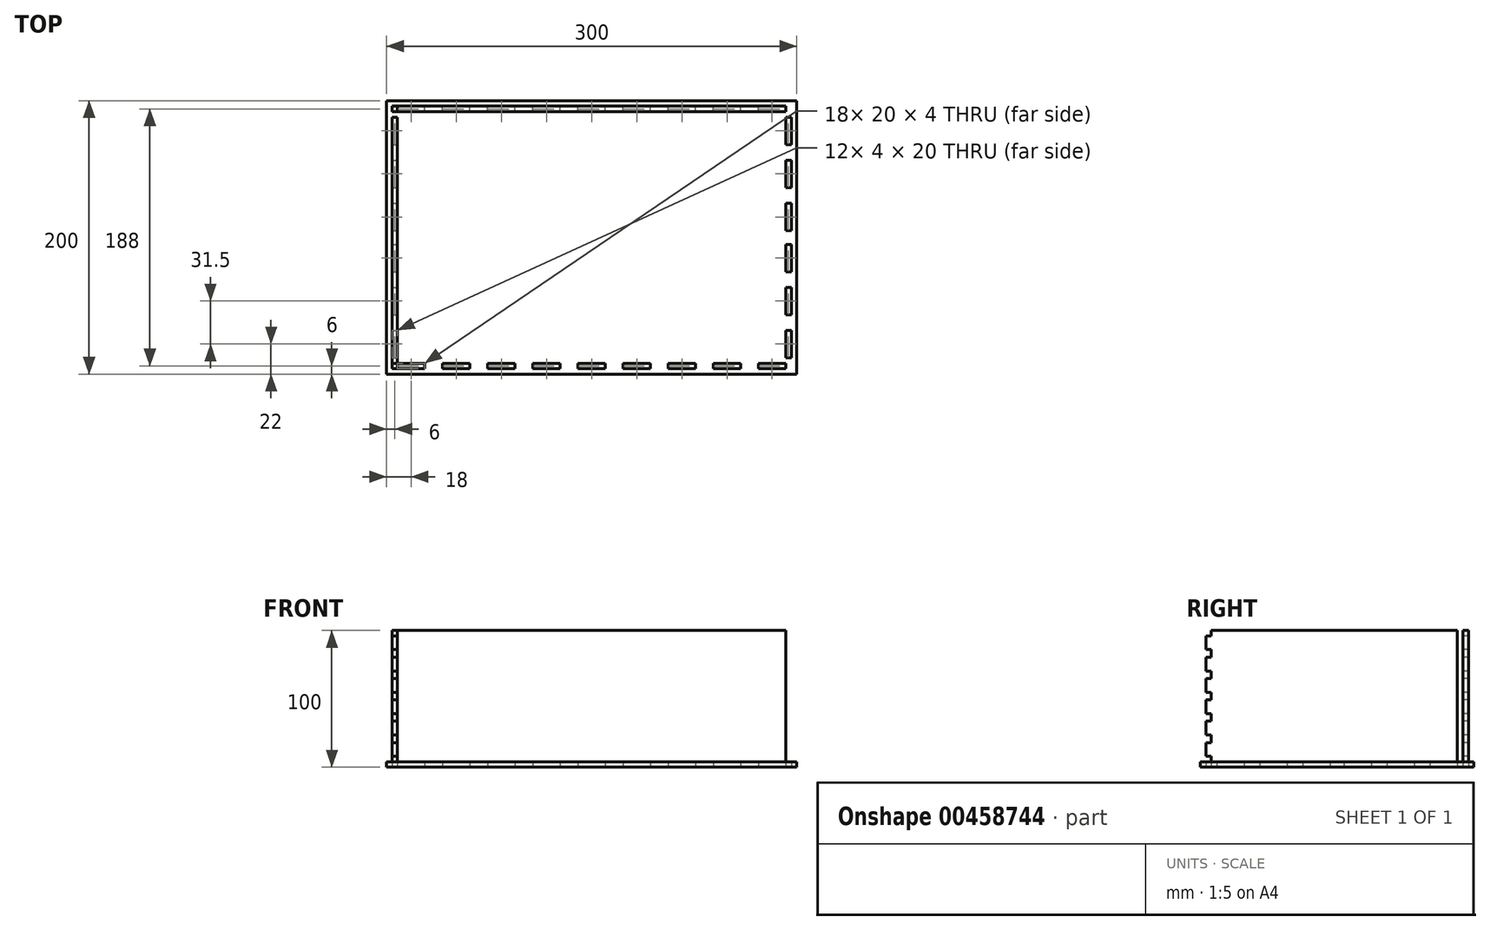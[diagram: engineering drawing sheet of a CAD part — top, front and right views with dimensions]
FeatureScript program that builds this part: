
annotation { "Feature Type Name" : "Feature", "Feature Type Description" : "" }
export const myFeature = defineFeature(function(context is Context, id is Id, definition is map)
    precondition{}
    {
        {
            assignVariable(context, id + "F0", {"name" : "w", "anyValue" : 4});
        }
        {
            var Q0;
            Q0=qCreatedBy(makeId("Top.planeOp"),FACE);
            var sketch = newSketch(context, id + "F1", { "sketchPlane" : qUnion([Q0])});
            skLineSegment(sketch, "E0.bottom", {"start": v(150, -100) * mm, "end": v(-150, -100) * mm});
            skLineSegment(sketch, "E0.top", {"start": v(150, 100) * mm, "end": v(-150, 100) * mm});
            skLineSegment(sketch, "E0.left", {"start": v(150, -100) * mm, "end": v(150, 100) * mm});
            skLineSegment(sketch, "E0.right", {"start": v(-150, -100) * mm, "end": v(-150, 100) * mm});
            skPoint(sketch, "E0.middle", {"position": v(0, 0) * mm});
            skLineSegment(sketch, "E1.0", {"start": v(142, 92) * mm, "end": v(-142, 92) * mm, "construction": true});
            skLineSegment(sketch, "E1.1", {"start": v(142, -92) * mm, "end": v(142, 92) * mm, "construction": true});
            skLineSegment(sketch, "E1.2", {"start": v(142, -92) * mm, "end": v(-142, -92) * mm, "construction": true});
            skLineSegment(sketch, "E1.3", {"start": v(-142, -92) * mm, "end": v(-142, 92) * mm, "construction": true});
            skLineSegment(sketch, "E2", {"start": v(-142, 0) * mm, "end": v(142, 0) * mm, "construction": true});
            skLineSegment(sketch, "E3", {"start": v(0, 92) * mm, "end": v(0, -92) * mm, "construction": true});
            skLineSegment(sketch, "E4.bottom", {"start": v(-142, 92) * mm, "end": v(-122, 92) * mm});
            skLineSegment(sketch, "E4.top", {"start": v(-142, 96) * mm, "end": v(-122, 96) * mm});
            skLineSegment(sketch, "E4.left", {"start": v(-142, 92) * mm, "end": v(-142, 96) * mm});
            skLineSegment(sketch, "E4.right", {"start": v(-122, 92) * mm, "end": v(-122, 96) * mm});
            skLineSegment(sketch, "E5.1.0.0", {"start": v(-109, 96) * mm, "end": v(-89, 96) * mm});
            skLineSegment(sketch, "E5.1.0.1", {"start": v(-109, 92) * mm, "end": v(-109, 96) * mm});
            skLineSegment(sketch, "E5.1.0.2", {"start": v(-89, 92) * mm, "end": v(-89, 96) * mm});
            skLineSegment(sketch, "E5.1.0.3", {"start": v(-109, 92) * mm, "end": v(-89, 92) * mm});
            skLineSegment(sketch, "E5.2.0.0", {"start": v(-76, 96) * mm, "end": v(-56, 96) * mm});
            skLineSegment(sketch, "E5.2.0.1", {"start": v(-76, 92) * mm, "end": v(-76, 96) * mm});
            skLineSegment(sketch, "E5.2.0.2", {"start": v(-56, 92) * mm, "end": v(-56, 96) * mm});
            skLineSegment(sketch, "E5.2.0.3", {"start": v(-76, 92) * mm, "end": v(-56, 92) * mm});
            skLineSegment(sketch, "E5.3.0.0", {"start": v(-43, 96) * mm, "end": v(-23, 96) * mm});
            skLineSegment(sketch, "E5.3.0.1", {"start": v(-43, 92) * mm, "end": v(-43, 96) * mm});
            skLineSegment(sketch, "E5.3.0.2", {"start": v(-23, 92) * mm, "end": v(-23, 96) * mm});
            skLineSegment(sketch, "E5.3.0.3", {"start": v(-43, 92) * mm, "end": v(-23, 92) * mm});
            skLineSegment(sketch, "E5.4.0.0", {"start": v(-10, 96) * mm, "end": v(10, 96) * mm});
            skLineSegment(sketch, "E5.4.0.1", {"start": v(-10, 92) * mm, "end": v(-10, 96) * mm});
            skLineSegment(sketch, "E5.4.0.2", {"start": v(10, 92) * mm, "end": v(10, 96) * mm});
            skLineSegment(sketch, "E5.4.0.3", {"start": v(-10, 92) * mm, "end": v(10, 92) * mm});
            skLineSegment(sketch, "E5.5.0.0", {"start": v(23, 96) * mm, "end": v(43, 96) * mm});
            skLineSegment(sketch, "E5.5.0.1", {"start": v(23, 92) * mm, "end": v(23, 96) * mm});
            skLineSegment(sketch, "E5.5.0.2", {"start": v(43, 92) * mm, "end": v(43, 96) * mm});
            skLineSegment(sketch, "E5.5.0.3", {"start": v(23, 92) * mm, "end": v(43, 92) * mm});
            skLineSegment(sketch, "E5.6.0.0", {"start": v(56, 96) * mm, "end": v(76, 96) * mm});
            skLineSegment(sketch, "E5.6.0.1", {"start": v(56, 92) * mm, "end": v(56, 96) * mm});
            skLineSegment(sketch, "E5.6.0.2", {"start": v(76, 92) * mm, "end": v(76, 96) * mm});
            skLineSegment(sketch, "E5.6.0.3", {"start": v(56, 92) * mm, "end": v(76, 92) * mm});
            skLineSegment(sketch, "E5.7.0.0", {"start": v(89, 96) * mm, "end": v(109, 96) * mm});
            skLineSegment(sketch, "E5.7.0.1", {"start": v(89, 92) * mm, "end": v(89, 96) * mm});
            skLineSegment(sketch, "E5.7.0.2", {"start": v(109, 92) * mm, "end": v(109, 96) * mm});
            skLineSegment(sketch, "E5.7.0.3", {"start": v(89, 92) * mm, "end": v(109, 92) * mm});
            skLineSegment(sketch, "E5.8.0.0", {"start": v(122, 96) * mm, "end": v(142, 96) * mm});
            skLineSegment(sketch, "E5.8.0.1", {"start": v(122, 92) * mm, "end": v(122, 96) * mm});
            skLineSegment(sketch, "E5.8.0.2", {"start": v(142, 92) * mm, "end": v(142, 96) * mm});
            skLineSegment(sketch, "E5.8.0.3", {"start": v(122, 92) * mm, "end": v(142, 92) * mm});
            skLineSegment(sketch, "E5.direction1", {"start": v(-142, 96) * mm, "end": v(-109, 96) * mm, "construction": true});
            skLineSegment(sketch, "E6.MirrorCS", {"start": v(-142, -92) * mm, "end": v(-142, -96) * mm});
            skLineSegment(sketch, "E7.MirrorCS", {"start": v(23, -92) * mm, "end": v(23, -96) * mm});
            skLineSegment(sketch, "E8.MirrorCS", {"start": v(-23, -92) * mm, "end": v(-23, -96) * mm});
            skLineSegment(sketch, "E9.MirrorCS", {"start": v(109, -92) * mm, "end": v(109, -96) * mm});
            skLineSegment(sketch, "E10.MirrorCS", {"start": v(10, -92) * mm, "end": v(10, -96) * mm});
            skLineSegment(sketch, "E11.MirrorCS", {"start": v(142, -92) * mm, "end": v(142, -96) * mm});
            skLineSegment(sketch, "E12.MirrorCS", {"start": v(43, -92) * mm, "end": v(43, -96) * mm});
            skLineSegment(sketch, "E13.MirrorCS", {"start": v(-89, -92) * mm, "end": v(-89, -96) * mm});
            skLineSegment(sketch, "E14.MirrorCS", {"start": v(76, -92) * mm, "end": v(76, -96) * mm});
            skLineSegment(sketch, "E15.MirrorCS", {"start": v(-56, -92) * mm, "end": v(-56, -96) * mm});
            skLineSegment(sketch, "E16.MirrorCS", {"start": v(-43, -92) * mm, "end": v(-43, -96) * mm});
            skLineSegment(sketch, "E17.MirrorCS", {"start": v(89, -92) * mm, "end": v(89, -96) * mm});
            skLineSegment(sketch, "E18.MirrorCS", {"start": v(-10, -92) * mm, "end": v(-10, -96) * mm});
            skLineSegment(sketch, "E19.MirrorCS", {"start": v(122, -92) * mm, "end": v(122, -96) * mm});
            skLineSegment(sketch, "E20.MirrorCS", {"start": v(-76, -92) * mm, "end": v(-76, -96) * mm});
            skLineSegment(sketch, "E21.MirrorCS", {"start": v(-109, -92) * mm, "end": v(-109, -96) * mm});
            skLineSegment(sketch, "E22.MirrorCS", {"start": v(-122, -92) * mm, "end": v(-122, -96) * mm});
            skLineSegment(sketch, "E23.MirrorCS", {"start": v(56, -92) * mm, "end": v(56, -96) * mm});
            skLineSegment(sketch, "E24.MirrorCS", {"start": v(-43, -92) * mm, "end": v(-23, -92) * mm});
            skLineSegment(sketch, "E25.MirrorCS", {"start": v(89, -92) * mm, "end": v(109, -92) * mm});
            skLineSegment(sketch, "E26.MirrorCS", {"start": v(23, -92) * mm, "end": v(43, -92) * mm});
            skLineSegment(sketch, "E27.MirrorCS", {"start": v(-109, -92) * mm, "end": v(-89, -92) * mm});
            skLineSegment(sketch, "E28.MirrorCS", {"start": v(56, -92) * mm, "end": v(76, -92) * mm});
            skLineSegment(sketch, "E29.MirrorCS", {"start": v(-76, -92) * mm, "end": v(-56, -92) * mm});
            skLineSegment(sketch, "E30.MirrorCS", {"start": v(-10, -92) * mm, "end": v(10, -92) * mm});
            skLineSegment(sketch, "E31.MirrorCS", {"start": v(122, -92) * mm, "end": v(142, -92) * mm});
            skLineSegment(sketch, "E32.MirrorCS", {"start": v(-142, -96) * mm, "end": v(-122, -96) * mm});
            skLineSegment(sketch, "E33.MirrorCS", {"start": v(-142, -92) * mm, "end": v(-122, -92) * mm});
            skLineSegment(sketch, "E34.MirrorCS", {"start": v(56, -96) * mm, "end": v(76, -96) * mm});
            skLineSegment(sketch, "E35.MirrorCS", {"start": v(-76, -96) * mm, "end": v(-56, -96) * mm});
            skLineSegment(sketch, "E36.MirrorCS", {"start": v(89, -96) * mm, "end": v(109, -96) * mm});
            skLineSegment(sketch, "E37.MirrorCS", {"start": v(-43, -96) * mm, "end": v(-23, -96) * mm});
            skLineSegment(sketch, "E38.MirrorCS", {"start": v(23, -96) * mm, "end": v(43, -96) * mm});
            skLineSegment(sketch, "E39.MirrorCS", {"start": v(-142, -96) * mm, "end": v(-109, -96) * mm, "construction": true});
            skLineSegment(sketch, "E40.MirrorCS", {"start": v(-10, -96) * mm, "end": v(10, -96) * mm});
            skLineSegment(sketch, "E41.MirrorCS", {"start": v(122, -96) * mm, "end": v(142, -96) * mm});
            skLineSegment(sketch, "E42.MirrorCS", {"start": v(-109, -96) * mm, "end": v(-89, -96) * mm});
            skLineSegment(sketch, "E43.bottom", {"start": v(-146, 88) * mm, "end": v(-142, 88) * mm});
            skLineSegment(sketch, "E43.top", {"start": v(-146, 68) * mm, "end": v(-142, 68) * mm});
            skLineSegment(sketch, "E43.left", {"start": v(-142, 88) * mm, "end": v(-142, 68) * mm});
            skLineSegment(sketch, "E43.right", {"start": v(-146, 88) * mm, "end": v(-146, 68) * mm});
            skLineSegment(sketch, "E44.0.1.0", {"start": v(-146, -5) * mm, "end": v(-146, -25) * mm});
            skLineSegment(sketch, "E44.0.1.1", {"start": v(-146, -5) * mm, "end": v(-142, -5) * mm});
            skLineSegment(sketch, "E44.0.1.2", {"start": v(-146, -25) * mm, "end": v(-142, -25) * mm});
            skLineSegment(sketch, "E44.0.1.3", {"start": v(-142, -5) * mm, "end": v(-142, -25) * mm});
            skLineSegment(sketch, "E44.1.0.0", {"start": v(-146, 56.5) * mm, "end": v(-146, 36.5) * mm});
            skLineSegment(sketch, "E44.1.0.1", {"start": v(-146, 56.5) * mm, "end": v(-142, 56.5) * mm});
            skLineSegment(sketch, "E44.1.0.2", {"start": v(-146, 36.5) * mm, "end": v(-142, 36.5) * mm});
            skLineSegment(sketch, "E44.1.0.3", {"start": v(-142, 56.5) * mm, "end": v(-142, 36.5) * mm});
            skLineSegment(sketch, "E44.1.1.0", {"start": v(-146, -36.5) * mm, "end": v(-146, -56.5) * mm});
            skLineSegment(sketch, "E44.1.1.1", {"start": v(-146, -36.5) * mm, "end": v(-142, -36.5) * mm});
            skLineSegment(sketch, "E44.1.1.2", {"start": v(-146, -56.5) * mm, "end": v(-142, -56.5) * mm});
            skLineSegment(sketch, "E44.1.1.3", {"start": v(-142, -36.5) * mm, "end": v(-142, -56.5) * mm});
            skLineSegment(sketch, "E44.2.0.0", {"start": v(-146, 25) * mm, "end": v(-146, 5) * mm});
            skLineSegment(sketch, "E44.2.0.1", {"start": v(-146, 25) * mm, "end": v(-142, 25) * mm});
            skLineSegment(sketch, "E44.2.0.2", {"start": v(-146, 5) * mm, "end": v(-142, 5) * mm});
            skLineSegment(sketch, "E44.2.0.3", {"start": v(-142, 25) * mm, "end": v(-142, 5) * mm});
            skLineSegment(sketch, "E44.2.1.0", {"start": v(-146, -68) * mm, "end": v(-146, -88) * mm});
            skLineSegment(sketch, "E44.2.1.1", {"start": v(-146, -68) * mm, "end": v(-142, -68) * mm});
            skLineSegment(sketch, "E44.2.1.2", {"start": v(-146, -88) * mm, "end": v(-142, -88) * mm});
            skLineSegment(sketch, "E44.2.1.3", {"start": v(-142, -68) * mm, "end": v(-142, -88) * mm});
            skLineSegment(sketch, "E44.direction1", {"start": v(-146, 68) * mm, "end": v(-146, 36.5) * mm, "construction": true});
            skLineSegment(sketch, "E44.direction2", {"start": v(-146, 68) * mm, "end": v(-146, -25) * mm, "construction": true});
            skLineSegment(sketch, "E45.MirrorCS", {"start": v(142, 92) * mm, "end": v(122, 92) * mm});
            skLineSegment(sketch, "E46.MirrorCS", {"start": v(146, -36.5) * mm, "end": v(142, -36.5) * mm});
            skLineSegment(sketch, "E47.MirrorCS", {"start": v(146, 56.5) * mm, "end": v(146, 36.5) * mm});
            skLineSegment(sketch, "E48.MirrorCS", {"start": v(146, -68) * mm, "end": v(142, -68) * mm});
            skLineSegment(sketch, "E49.MirrorCS", {"start": v(146, -5) * mm, "end": v(142, -5) * mm});
            skLineSegment(sketch, "E50.MirrorCS", {"start": v(146, 88) * mm, "end": v(142, 88) * mm});
            skLineSegment(sketch, "E51.MirrorCS", {"start": v(146, 56.5) * mm, "end": v(142, 56.5) * mm});
            skLineSegment(sketch, "E52.MirrorCS", {"start": v(146, -25) * mm, "end": v(142, -25) * mm});
            skLineSegment(sketch, "E53.MirrorCS", {"start": v(146, -88) * mm, "end": v(142, -88) * mm});
            skLineSegment(sketch, "E54.MirrorCS", {"start": v(146, -56.5) * mm, "end": v(142, -56.5) * mm});
            skLineSegment(sketch, "E55.MirrorCS", {"start": v(146, 68) * mm, "end": v(142, 68) * mm});
            skLineSegment(sketch, "E56.MirrorCS", {"start": v(146, 25) * mm, "end": v(142, 25) * mm});
            skLineSegment(sketch, "E57.MirrorCS", {"start": v(146, 36.5) * mm, "end": v(142, 36.5) * mm});
            skLineSegment(sketch, "E58.MirrorCS", {"start": v(146, 5) * mm, "end": v(142, 5) * mm});
            skLineSegment(sketch, "E59.MirrorCS", {"start": v(-142, 92) * mm, "end": v(142, 92) * mm, "construction": true});
            skLineSegment(sketch, "E60.MirrorCS", {"start": v(146, 68) * mm, "end": v(146, 36.5) * mm, "construction": true});
            skLineSegment(sketch, "E61.MirrorCS", {"start": v(146, 25) * mm, "end": v(146, 5) * mm});
            skLineSegment(sketch, "E62.MirrorCS", {"start": v(146, -5) * mm, "end": v(146, -25) * mm});
            skLineSegment(sketch, "E63.MirrorCS", {"start": v(142, -36.5) * mm, "end": v(142, -56.5) * mm});
            skLineSegment(sketch, "E64.MirrorCS", {"start": v(142, -5) * mm, "end": v(142, -25) * mm});
            skLineSegment(sketch, "E65.MirrorCS", {"start": v(142, -68) * mm, "end": v(142, -88) * mm});
            skLineSegment(sketch, "E66.MirrorCS", {"start": v(146, 68) * mm, "end": v(146, -25) * mm, "construction": true});
            skLineSegment(sketch, "E67.MirrorCS", {"start": v(146, -68) * mm, "end": v(146, -88) * mm});
            skLineSegment(sketch, "E68.MirrorCS", {"start": v(146, -36.5) * mm, "end": v(146, -56.5) * mm});
            skLineSegment(sketch, "E69.MirrorCS", {"start": v(146, 88) * mm, "end": v(146, 68) * mm});
            skLineSegment(sketch, "E70.MirrorCS", {"start": v(142, 25) * mm, "end": v(142, 5) * mm});
            skLineSegment(sketch, "E71.MirrorCS", {"start": v(142, 56.5) * mm, "end": v(142, 36.5) * mm});
            skLineSegment(sketch, "E72.MirrorCS", {"start": v(142, 88) * mm, "end": v(142, 68) * mm});
            skSolve(sketch);
        }
        {
            var Q0;
            Q0=makeQuery(id+"F1.imprint","IMPRINT",FACE,{"disambiguationData":[TD([[makeQuery(id+"F1.imprint","IMPRINT",EDGE,{"derivedFrom":sQuery(id+"F1.wireOp",EDGE,"E0.bottom")}),-1.0]])]});
            extrude(context, id + "F2", {"entities" : qUnion([Q0]), "depth" : (getVariable(context, 'w')) * mm});
        }
        {
            var Q0;
            Q0=makeQuery(id+"F1.imprint","IMPRINT",FACE,{"disambiguationData":[TD([[makeQuery(id+"F1.imprint","IMPRINT",EDGE,{"derivedFrom":sQuery(id+"F1.wireOp",EDGE,"E4.bottom")}),1.0]])]});
            var Q1;
            Q1=makeQuery(id+"F1.imprint","IMPRINT",FACE,{"disambiguationData":[TD([[makeQuery(id+"F1.imprint","IMPRINT",EDGE,{"derivedFrom":sQuery(id+"F1.wireOp",EDGE,"E5.1.0.0")}),-1.0]])]});
            var Q2;
            Q2=makeQuery(id+"F1.imprint","IMPRINT",FACE,{"disambiguationData":[TD([[makeQuery(id+"F1.imprint","IMPRINT",EDGE,{"derivedFrom":sQuery(id+"F1.wireOp",EDGE,"E5.2.0.0")}),-1.0]])]});
            var Q3;
            Q3=makeQuery(id+"F1.imprint","IMPRINT",FACE,{"disambiguationData":[TD([[makeQuery(id+"F1.imprint","IMPRINT",EDGE,{"derivedFrom":sQuery(id+"F1.wireOp",EDGE,"E5.3.0.0")}),-1.0]])]});
            var Q4;
            Q4=makeQuery(id+"F1.imprint","IMPRINT",FACE,{"disambiguationData":[TD([[makeQuery(id+"F1.imprint","IMPRINT",EDGE,{"derivedFrom":sQuery(id+"F1.wireOp",EDGE,"E5.4.0.0")}),-1.0]])]});
            var Q5;
            Q5=makeQuery(id+"F1.imprint","IMPRINT",FACE,{"disambiguationData":[TD([[makeQuery(id+"F1.imprint","IMPRINT",EDGE,{"derivedFrom":sQuery(id+"F1.wireOp",EDGE,"E5.5.0.0")}),-1.0]])]});
            var Q6;
            Q6=makeQuery(id+"F1.imprint","IMPRINT",FACE,{"disambiguationData":[TD([[makeQuery(id+"F1.imprint","IMPRINT",EDGE,{"derivedFrom":sQuery(id+"F1.wireOp",EDGE,"E5.6.0.0")}),-1.0]])]});
            var Q7;
            Q7=makeQuery(id+"F1.imprint","IMPRINT",FACE,{"disambiguationData":[TD([[makeQuery(id+"F1.imprint","IMPRINT",EDGE,{"derivedFrom":sQuery(id+"F1.wireOp",EDGE,"E5.7.0.0")}),-1.0]])]});
            var Q8;
            Q8=makeQuery(id+"F1.imprint","IMPRINT",FACE,{"disambiguationData":[TD([[makeQuery(id+"F1.imprint","IMPRINT",EDGE,{"derivedFrom":sQuery(id+"F1.wireOp",EDGE,"E5.8.0.0")}),-1.0]])]});
            extrude(context, id + "F3", {"entities" : qUnion([Q0, Q1, Q2, Q3, Q4, Q5, Q6, Q7, Q8]), "depth" : (getVariable(context, 'w')) * mm});
        }
        {
            var Q0;
            Q0=makeQuery(id+"F2.opExtrude","CAP_FACE",FACE,{"disambiguationData":[OSD([sQuery(id+"F1.wireOp",EDGE,"E0.bottom"),sQuery(id+"F1.wireOp",EDGE,"E0.top"),sQuery(id+"F1.wireOp",EDGE,"E0.left"),sQuery(id+"F1.wireOp",EDGE,"E0.right"),sQuery(id+"F1.wireOp",EDGE,"E4.bottom"),sQuery(id+"F1.wireOp",EDGE,"E4.top"),sQuery(id+"F1.wireOp",EDGE,"E4.left"),sQuery(id+"F1.wireOp",EDGE,"E4.right"),sQuery(id+"F1.wireOp",EDGE,"E5.1.0.0"),sQuery(id+"F1.wireOp",EDGE,"E5.1.0.1"),sQuery(id+"F1.wireOp",EDGE,"E5.1.0.2"),sQuery(id+"F1.wireOp",EDGE,"E5.1.0.3"),sQuery(id+"F1.wireOp",EDGE,"E5.2.0.0"),sQuery(id+"F1.wireOp",EDGE,"E5.2.0.1"),sQuery(id+"F1.wireOp",EDGE,"E5.2.0.2"),sQuery(id+"F1.wireOp",EDGE,"E5.2.0.3"),sQuery(id+"F1.wireOp",EDGE,"E5.3.0.0"),sQuery(id+"F1.wireOp",EDGE,"E5.3.0.1"),sQuery(id+"F1.wireOp",EDGE,"E5.3.0.2"),sQuery(id+"F1.wireOp",EDGE,"E5.3.0.3"),sQuery(id+"F1.wireOp",EDGE,"E5.4.0.0"),sQuery(id+"F1.wireOp",EDGE,"E5.4.0.1"),sQuery(id+"F1.wireOp",EDGE,"E5.4.0.2"),sQuery(id+"F1.wireOp",EDGE,"E5.4.0.3"),sQuery(id+"F1.wireOp",EDGE,"E5.5.0.0"),sQuery(id+"F1.wireOp",EDGE,"E5.5.0.1"),sQuery(id+"F1.wireOp",EDGE,"E5.5.0.2"),sQuery(id+"F1.wireOp",EDGE,"E5.5.0.3"),sQuery(id+"F1.wireOp",EDGE,"E5.6.0.0"),sQuery(id+"F1.wireOp",EDGE,"E5.6.0.1"),sQuery(id+"F1.wireOp",EDGE,"E5.6.0.2"),sQuery(id+"F1.wireOp",EDGE,"E5.6.0.3"),sQuery(id+"F1.wireOp",EDGE,"E5.7.0.0"),sQuery(id+"F1.wireOp",EDGE,"E5.7.0.1"),sQuery(id+"F1.wireOp",EDGE,"E5.7.0.2"),sQuery(id+"F1.wireOp",EDGE,"E5.7.0.3"),sQuery(id+"F1.wireOp",EDGE,"E5.8.0.0"),sQuery(id+"F1.wireOp",EDGE,"E5.8.0.1"),sQuery(id+"F1.wireOp",EDGE,"E5.8.0.2"),sQuery(id+"F1.wireOp",EDGE,"E6.MirrorCS"),sQuery(id+"F1.wireOp",EDGE,"E7.MirrorCS"),sQuery(id+"F1.wireOp",EDGE,"E8.MirrorCS"),sQuery(id+"F1.wireOp",EDGE,"E9.MirrorCS"),sQuery(id+"F1.wireOp",EDGE,"E10.MirrorCS"),sQuery(id+"F1.wireOp",EDGE,"E11.MirrorCS"),sQuery(id+"F1.wireOp",EDGE,"E12.MirrorCS"),sQuery(id+"F1.wireOp",EDGE,"E13.MirrorCS"),sQuery(id+"F1.wireOp",EDGE,"E14.MirrorCS"),sQuery(id+"F1.wireOp",EDGE,"E15.MirrorCS"),sQuery(id+"F1.wireOp",EDGE,"E16.MirrorCS"),sQuery(id+"F1.wireOp",EDGE,"E17.MirrorCS"),sQuery(id+"F1.wireOp",EDGE,"E18.MirrorCS"),sQuery(id+"F1.wireOp",EDGE,"E19.MirrorCS"),sQuery(id+"F1.wireOp",EDGE,"E20.MirrorCS"),sQuery(id+"F1.wireOp",EDGE,"E21.MirrorCS"),sQuery(id+"F1.wireOp",EDGE,"E22.MirrorCS"),sQuery(id+"F1.wireOp",EDGE,"E23.MirrorCS"),sQuery(id+"F1.wireOp",EDGE,"E24.MirrorCS"),sQuery(id+"F1.wireOp",EDGE,"E25.MirrorCS"),sQuery(id+"F1.wireOp",EDGE,"E26.MirrorCS"),sQuery(id+"F1.wireOp",EDGE,"E27.MirrorCS"),sQuery(id+"F1.wireOp",EDGE,"E28.MirrorCS"),sQuery(id+"F1.wireOp",EDGE,"E29.MirrorCS"),sQuery(id+"F1.wireOp",EDGE,"E30.MirrorCS"),sQuery(id+"F1.wireOp",EDGE,"E31.MirrorCS"),sQuery(id+"F1.wireOp",EDGE,"E32.MirrorCS"),sQuery(id+"F1.wireOp",EDGE,"E33.MirrorCS"),sQuery(id+"F1.wireOp",EDGE,"E34.MirrorCS"),sQuery(id+"F1.wireOp",EDGE,"E35.MirrorCS"),sQuery(id+"F1.wireOp",EDGE,"E36.MirrorCS"),sQuery(id+"F1.wireOp",EDGE,"E37.MirrorCS"),sQuery(id+"F1.wireOp",EDGE,"E38.MirrorCS"),sQuery(id+"F1.wireOp",EDGE,"E40.MirrorCS"),sQuery(id+"F1.wireOp",EDGE,"E41.MirrorCS"),sQuery(id+"F1.wireOp",EDGE,"E42.MirrorCS"),sQuery(id+"F1.wireOp",EDGE,"E43.bottom"),sQuery(id+"F1.wireOp",EDGE,"E43.top"),sQuery(id+"F1.wireOp",EDGE,"E43.left"),sQuery(id+"F1.wireOp",EDGE,"E43.right"),sQuery(id+"F1.wireOp",EDGE,"E44.0.1.0"),sQuery(id+"F1.wireOp",EDGE,"E44.0.1.1"),sQuery(id+"F1.wireOp",EDGE,"E44.0.1.2"),sQuery(id+"F1.wireOp",EDGE,"E44.0.1.3"),sQuery(id+"F1.wireOp",EDGE,"E44.1.0.0"),sQuery(id+"F1.wireOp",EDGE,"E44.1.0.1"),sQuery(id+"F1.wireOp",EDGE,"E44.1.0.2"),sQuery(id+"F1.wireOp",EDGE,"E44.1.0.3"),sQuery(id+"F1.wireOp",EDGE,"E44.1.1.0"),sQuery(id+"F1.wireOp",EDGE,"E44.1.1.1"),sQuery(id+"F1.wireOp",EDGE,"E44.1.1.2"),sQuery(id+"F1.wireOp",EDGE,"E44.1.1.3"),sQuery(id+"F1.wireOp",EDGE,"E44.2.0.0"),sQuery(id+"F1.wireOp",EDGE,"E44.2.0.1"),sQuery(id+"F1.wireOp",EDGE,"E44.2.0.2"),sQuery(id+"F1.wireOp",EDGE,"E44.2.0.3"),sQuery(id+"F1.wireOp",EDGE,"E44.2.1.0"),sQuery(id+"F1.wireOp",EDGE,"E44.2.1.1"),sQuery(id+"F1.wireOp",EDGE,"E44.2.1.2"),sQuery(id+"F1.wireOp",EDGE,"E44.2.1.3"),sQuery(id+"F1.wireOp",EDGE,"E45.MirrorCS"),sQuery(id+"F1.wireOp",EDGE,"E46.MirrorCS"),sQuery(id+"F1.wireOp",EDGE,"E47.MirrorCS"),sQuery(id+"F1.wireOp",EDGE,"E48.MirrorCS"),sQuery(id+"F1.wireOp",EDGE,"E49.MirrorCS"),sQuery(id+"F1.wireOp",EDGE,"E50.MirrorCS"),sQuery(id+"F1.wireOp",EDGE,"E51.MirrorCS"),sQuery(id+"F1.wireOp",EDGE,"E52.MirrorCS"),sQuery(id+"F1.wireOp",EDGE,"E53.MirrorCS"),sQuery(id+"F1.wireOp",EDGE,"E54.MirrorCS"),sQuery(id+"F1.wireOp",EDGE,"E55.MirrorCS"),sQuery(id+"F1.wireOp",EDGE,"E56.MirrorCS"),sQuery(id+"F1.wireOp",EDGE,"E57.MirrorCS"),sQuery(id+"F1.wireOp",EDGE,"E58.MirrorCS"),sQuery(id+"F1.wireOp",EDGE,"E61.MirrorCS"),sQuery(id+"F1.wireOp",EDGE,"E62.MirrorCS"),sQuery(id+"F1.wireOp",EDGE,"E63.MirrorCS"),sQuery(id+"F1.wireOp",EDGE,"E64.MirrorCS"),sQuery(id+"F1.wireOp",EDGE,"E65.MirrorCS"),sQuery(id+"F1.wireOp",EDGE,"E67.MirrorCS"),sQuery(id+"F1.wireOp",EDGE,"E68.MirrorCS"),sQuery(id+"F1.wireOp",EDGE,"E69.MirrorCS"),sQuery(id+"F1.wireOp",EDGE,"E70.MirrorCS"),sQuery(id+"F1.wireOp",EDGE,"E71.MirrorCS"),sQuery(id+"F1.wireOp",EDGE,"E72.MirrorCS")])],"isStart":false});
            var sketch = newSketch(context, id + "F4", { "sketchPlane" : qUnion([Q0])});
            skLineSegment(sketch, "E73.0", {"start": v(-142, 56.5) * mm, "end": v(-142, 36.5) * mm});
            skLineSegment(sketch, "E73.1", {"start": v(150, -100) * mm, "end": v(-150, -100) * mm});
            skLineSegment(sketch, "E73.2", {"start": v(-142, 0) * mm, "end": v(142, 0) * mm});
            skLineSegment(sketch, "E73.3", {"start": v(-142, 92) * mm, "end": v(-122, 92) * mm});
            skLineSegment(sketch, "E73.4", {"start": v(56, -96) * mm, "end": v(76, -96) * mm});
            skLineSegment(sketch, "E73.5", {"start": v(150, 100) * mm, "end": v(-150, 100) * mm});
            skLineSegment(sketch, "E73.6", {"start": v(-150, -100) * mm, "end": v(-150, 100) * mm});
            skLineSegment(sketch, "E73.7", {"start": v(-142, -68) * mm, "end": v(-142, -88) * mm});
            skLineSegment(sketch, "E73.8", {"start": v(146, 25) * mm, "end": v(146, 5) * mm});
            skLineSegment(sketch, "E73.9", {"start": v(142, -36.5) * mm, "end": v(142, -56.5) * mm});
            skLineSegment(sketch, "E73.10", {"start": v(142, -92) * mm, "end": v(-142, -92) * mm});
            skLineSegment(sketch, "E73.11", {"start": v(-10, 92) * mm, "end": v(10, 92) * mm});
            skLineSegment(sketch, "E73.12", {"start": v(23, -96) * mm, "end": v(43, -96) * mm});
            skLineSegment(sketch, "E73.13", {"start": v(-43, -96) * mm, "end": v(-23, -96) * mm});
            skLineSegment(sketch, "E73.14", {"start": v(146, 56.5) * mm, "end": v(146, 36.5) * mm});
            skLineSegment(sketch, "E73.15", {"start": v(142, -92) * mm, "end": v(142, 92) * mm});
            skLineSegment(sketch, "E73.16", {"start": v(0, 92) * mm, "end": v(0, -92) * mm});
            skLineSegment(sketch, "E73.17", {"start": v(142, 92) * mm, "end": v(-142, 92) * mm});
            skLineSegment(sketch, "E73.18", {"start": v(23, 96) * mm, "end": v(43, 96) * mm});
            skLineSegment(sketch, "E73.19", {"start": v(-142, 96) * mm, "end": v(-122, 96) * mm});
            skLineSegment(sketch, "E73.20", {"start": v(-142, -92) * mm, "end": v(-142, 92) * mm});
            skLineSegment(sketch, "E73.21", {"start": v(142, 92) * mm, "end": v(122, 92) * mm});
            skLineSegment(sketch, "E73.22", {"start": v(-146, 68) * mm, "end": v(-146, -25) * mm});
            skLineSegment(sketch, "E73.23", {"start": v(-109, 96) * mm, "end": v(-89, 96) * mm});
            skLineSegment(sketch, "E73.24", {"start": v(-146, 68) * mm, "end": v(-146, 36.5) * mm});
            skLineSegment(sketch, "E73.25", {"start": v(89, -96) * mm, "end": v(109, -96) * mm});
            skLineSegment(sketch, "E73.26", {"start": v(-76, -96) * mm, "end": v(-56, -96) * mm});
            skLineSegment(sketch, "E73.27", {"start": v(-142, 96) * mm, "end": v(-109, 96) * mm});
            skLineSegment(sketch, "E73.28", {"start": v(-146, -36.5) * mm, "end": v(-146, -56.5) * mm});
            skLineSegment(sketch, "E73.29", {"start": v(122, 96) * mm, "end": v(142, 96) * mm});
            skLineSegment(sketch, "E73.30", {"start": v(23, 92) * mm, "end": v(43, 92) * mm});
            skLineSegment(sketch, "E73.31", {"start": v(-10, 96) * mm, "end": v(10, 96) * mm});
            skLineSegment(sketch, "E73.32", {"start": v(-142, -92) * mm, "end": v(-122, -92) * mm});
            skLineSegment(sketch, "E73.33", {"start": v(-142, 25) * mm, "end": v(-142, 5) * mm});
            skLineSegment(sketch, "E73.34", {"start": v(-109, 92) * mm, "end": v(-89, 92) * mm});
            skLineSegment(sketch, "E73.35", {"start": v(-10, -96) * mm, "end": v(10, -96) * mm});
            skLineSegment(sketch, "E73.36", {"start": v(-142, 88) * mm, "end": v(-142, 68) * mm});
            skLineSegment(sketch, "E73.37", {"start": v(142, -5) * mm, "end": v(142, -25) * mm});
            skLineSegment(sketch, "E73.38", {"start": v(-76, 96) * mm, "end": v(-56, 96) * mm});
            skLineSegment(sketch, "E73.39", {"start": v(-142, -96) * mm, "end": v(-122, -96) * mm});
            skLineSegment(sketch, "E73.40", {"start": v(89, -92) * mm, "end": v(109, -92) * mm});
            skLineSegment(sketch, "E73.41", {"start": v(142, -68) * mm, "end": v(142, -88) * mm});
            skLineSegment(sketch, "E73.42", {"start": v(56, 96) * mm, "end": v(76, 96) * mm});
            skLineSegment(sketch, "E73.43", {"start": v(-43, 92) * mm, "end": v(-23, 92) * mm});
            skLineSegment(sketch, "E73.44", {"start": v(-142, -5) * mm, "end": v(-142, -25) * mm});
            skLineSegment(sketch, "E73.45", {"start": v(150, -100) * mm, "end": v(150, 100) * mm});
            skLineSegment(sketch, "E73.46", {"start": v(-146, 56.5) * mm, "end": v(-146, 36.5) * mm});
            skLineSegment(sketch, "E73.47", {"start": v(146, 68) * mm, "end": v(146, -25) * mm});
            skLineSegment(sketch, "E73.48", {"start": v(-146, 25) * mm, "end": v(-146, 5) * mm});
            skLineSegment(sketch, "E73.49", {"start": v(-76, 92) * mm, "end": v(-56, 92) * mm});
            skLineSegment(sketch, "E73.50", {"start": v(146, -36.5) * mm, "end": v(146, -56.5) * mm});
            skLineSegment(sketch, "E73.51", {"start": v(56, 92) * mm, "end": v(76, 92) * mm});
            skLineSegment(sketch, "E73.52", {"start": v(89, 96) * mm, "end": v(109, 96) * mm});
            skLineSegment(sketch, "E73.53", {"start": v(-76, -92) * mm, "end": v(-56, -92) * mm});
            skLineSegment(sketch, "E73.54", {"start": v(-146, -68) * mm, "end": v(-146, -88) * mm});
            skLineSegment(sketch, "E73.55", {"start": v(142, 56.5) * mm, "end": v(142, 36.5) * mm});
            skLineSegment(sketch, "E73.56", {"start": v(122, -92) * mm, "end": v(142, -92) * mm});
            skLineSegment(sketch, "E73.57", {"start": v(-43, 96) * mm, "end": v(-23, 96) * mm});
            skLineSegment(sketch, "E73.58", {"start": v(-146, 88) * mm, "end": v(-146, 68) * mm});
            skLineSegment(sketch, "E73.59", {"start": v(142, 88) * mm, "end": v(142, 68) * mm});
            skLineSegment(sketch, "E73.60", {"start": v(-142, -96) * mm, "end": v(-109, -96) * mm});
            skLineSegment(sketch, "E73.61", {"start": v(146, -5) * mm, "end": v(146, -25) * mm});
            skLineSegment(sketch, "E73.62", {"start": v(146, 68) * mm, "end": v(146, 36.5) * mm});
            skLineSegment(sketch, "E73.63", {"start": v(122, -96) * mm, "end": v(142, -96) * mm});
            skLineSegment(sketch, "E73.64", {"start": v(-43, -92) * mm, "end": v(-23, -92) * mm});
            skLineSegment(sketch, "E73.65", {"start": v(-142, -36.5) * mm, "end": v(-142, -56.5) * mm});
            skLineSegment(sketch, "E73.66", {"start": v(23, -92) * mm, "end": v(43, -92) * mm});
            skLineSegment(sketch, "E73.67", {"start": v(-109, -92) * mm, "end": v(-89, -92) * mm});
            skLineSegment(sketch, "E73.68", {"start": v(146, 88) * mm, "end": v(146, 68) * mm});
            skLineSegment(sketch, "E73.69", {"start": v(146, -68) * mm, "end": v(146, -88) * mm});
            skLineSegment(sketch, "E73.70", {"start": v(56, -92) * mm, "end": v(76, -92) * mm});
            skLineSegment(sketch, "E73.71", {"start": v(142, 25) * mm, "end": v(142, 5) * mm});
            skLineSegment(sketch, "E73.72", {"start": v(-109, -96) * mm, "end": v(-89, -96) * mm});
            skLineSegment(sketch, "E73.73", {"start": v(-146, -5) * mm, "end": v(-146, -25) * mm});
            skLineSegment(sketch, "E73.74", {"start": v(-10, -92) * mm, "end": v(10, -92) * mm});
            skLineSegment(sketch, "E73.75", {"start": v(89, 92) * mm, "end": v(109, 92) * mm});
            skLineSegment(sketch, "E73.76", {"start": v(150, -100) * mm, "end": v(-150, -100) * mm});
            skLineSegment(sketch, "E73.77", {"start": v(-150, -100) * mm, "end": v(-150, 100) * mm});
            skLineSegment(sketch, "E73.78", {"start": v(150, 100) * mm, "end": v(-150, 100) * mm});
            skLineSegment(sketch, "E73.79", {"start": v(150, -100) * mm, "end": v(150, 100) * mm});
            skLineSegment(sketch, "E73.80", {"start": v(-142, 92) * mm, "end": v(142, 92) * mm});
            skLineSegment(sketch, "E73.81", {"start": v(122, 92) * mm, "end": v(142, 92) * mm});
            skLineSegment(sketch, "E74.bottom", {"start": v(-150, 96) * mm, "end": v(150, 96) * mm});
            skLineSegment(sketch, "E74.top", {"start": v(-150, 92) * mm, "end": v(150, 92) * mm});
            skLineSegment(sketch, "E74.left", {"start": v(-150, 96) * mm, "end": v(-150, 92) * mm});
            skLineSegment(sketch, "E74.right", {"start": v(150, 96) * mm, "end": v(150, 92) * mm});
            skLineSegment(sketch, "E75.bottom", {"start": v(-142, 92) * mm, "end": v(-146, 92) * mm});
            skLineSegment(sketch, "E75.top", {"start": v(-142, -92) * mm, "end": v(-146, -92) * mm});
            skLineSegment(sketch, "E75.left", {"start": v(-142, 92) * mm, "end": v(-142, -92) * mm});
            skLineSegment(sketch, "E75.right", {"start": v(-146, 92) * mm, "end": v(-146, -92) * mm});
            skSolve(sketch);
        }
        {
            var Q0;
            {var subQ1=sQuery(id+"F4.wireOp",EDGE,"E74.left");Q0=makeQuery(id+"F4.imprint","IMPRINT",FACE,{"disambiguationData":[TD([[makeQuery(id+"F4.imprint","IMPRINT",EDGE,{"derivedFrom":subQ1}),-1.0]])]});}
            var Q1;
            {var subQ1=makeQuery(id+"F2.opExtrude","CAP_EDGE",EDGE,{"disambiguationData":[OSD([sQuery(id+"F1.wireOp",EDGE,"E4.left")])],"isStart":false});Q1=makeQuery(id+"F4.imprint","IMPRINT",FACE,{"disambiguationData":[TD([[makeQuery(id+"F4.imprint","IMPRINT",EDGE,{"derivedFrom":subQ1}),-1.0]])]});}
            var Q2;
            {var subQ1=makeQuery(id+"F2.opExtrude","CAP_EDGE",EDGE,{"disambiguationData":[OSD([sQuery(id+"F1.wireOp",EDGE,"E4.right")])],"isStart":false});Q2=makeQuery(id+"F4.imprint","IMPRINT",FACE,{"disambiguationData":[TD([[makeQuery(id+"F4.imprint","IMPRINT",EDGE,{"derivedFrom":subQ1}),-1.0]])]});}
            var Q3;
            {var subQ1=makeQuery(id+"F2.opExtrude","CAP_EDGE",EDGE,{"disambiguationData":[OSD([sQuery(id+"F1.wireOp",EDGE,"E5.1.0.1")])],"isStart":false});Q3=makeQuery(id+"F4.imprint","IMPRINT",FACE,{"disambiguationData":[TD([[makeQuery(id+"F4.imprint","IMPRINT",EDGE,{"derivedFrom":subQ1}),-1.0]])]});}
            var Q4;
            {var subQ1=makeQuery(id+"F2.opExtrude","CAP_EDGE",EDGE,{"disambiguationData":[OSD([sQuery(id+"F1.wireOp",EDGE,"E5.1.0.2")])],"isStart":false});Q4=makeQuery(id+"F4.imprint","IMPRINT",FACE,{"disambiguationData":[TD([[makeQuery(id+"F4.imprint","IMPRINT",EDGE,{"derivedFrom":subQ1}),-1.0]])]});}
            var Q5;
            {var subQ1=makeQuery(id+"F2.opExtrude","CAP_EDGE",EDGE,{"disambiguationData":[OSD([sQuery(id+"F1.wireOp",EDGE,"E5.2.0.1")])],"isStart":false});Q5=makeQuery(id+"F4.imprint","IMPRINT",FACE,{"disambiguationData":[TD([[makeQuery(id+"F4.imprint","IMPRINT",EDGE,{"derivedFrom":subQ1}),-1.0]])]});}
            var Q6;
            {var subQ1=makeQuery(id+"F2.opExtrude","CAP_EDGE",EDGE,{"disambiguationData":[OSD([sQuery(id+"F1.wireOp",EDGE,"E5.2.0.2")])],"isStart":false});Q6=makeQuery(id+"F4.imprint","IMPRINT",FACE,{"disambiguationData":[TD([[makeQuery(id+"F4.imprint","IMPRINT",EDGE,{"derivedFrom":subQ1}),-1.0]])]});}
            var Q7;
            {var subQ1=makeQuery(id+"F2.opExtrude","CAP_EDGE",EDGE,{"disambiguationData":[OSD([sQuery(id+"F1.wireOp",EDGE,"E5.3.0.1")])],"isStart":false});Q7=makeQuery(id+"F4.imprint","IMPRINT",FACE,{"disambiguationData":[TD([[makeQuery(id+"F4.imprint","IMPRINT",EDGE,{"derivedFrom":subQ1}),-1.0]])]});}
            var Q8;
            {var subQ1=makeQuery(id+"F2.opExtrude","CAP_EDGE",EDGE,{"disambiguationData":[OSD([sQuery(id+"F1.wireOp",EDGE,"E5.3.0.2")])],"isStart":false});Q8=makeQuery(id+"F4.imprint","IMPRINT",FACE,{"disambiguationData":[TD([[makeQuery(id+"F4.imprint","IMPRINT",EDGE,{"derivedFrom":subQ1}),-1.0]])]});}
            var Q9;
            {var subQ0=makeQuery(id+"F2.opExtrude","CAP_EDGE",EDGE,{"disambiguationData":[OSD([sQuery(id+"F1.wireOp",EDGE,"E5.4.0.1")])],"isStart":false});Q9=makeQuery(id+"F4.imprint","IMPRINT",FACE,{"disambiguationData":[TD([[makeQuery(id+"F4.imprint","IMPRINT",EDGE,{"derivedFrom":subQ0}),-1.0]])]});}
            var Q10;
            {var subQ1=makeQuery(id+"F2.opExtrude","CAP_EDGE",EDGE,{"disambiguationData":[OSD([sQuery(id+"F1.wireOp",EDGE,"E5.4.0.2")])],"isStart":false});Q10=makeQuery(id+"F4.imprint","IMPRINT",FACE,{"disambiguationData":[TD([[makeQuery(id+"F4.imprint","IMPRINT",EDGE,{"derivedFrom":subQ1}),-1.0]])]});}
            var Q11;
            {var subQ1=makeQuery(id+"F2.opExtrude","CAP_EDGE",EDGE,{"disambiguationData":[OSD([sQuery(id+"F1.wireOp",EDGE,"E5.5.0.1")])],"isStart":false});Q11=makeQuery(id+"F4.imprint","IMPRINT",FACE,{"disambiguationData":[TD([[makeQuery(id+"F4.imprint","IMPRINT",EDGE,{"derivedFrom":subQ1}),-1.0]])]});}
            var Q12;
            {var subQ1=makeQuery(id+"F2.opExtrude","CAP_EDGE",EDGE,{"disambiguationData":[OSD([sQuery(id+"F1.wireOp",EDGE,"E5.5.0.2")])],"isStart":false});Q12=makeQuery(id+"F4.imprint","IMPRINT",FACE,{"disambiguationData":[TD([[makeQuery(id+"F4.imprint","IMPRINT",EDGE,{"derivedFrom":subQ1}),-1.0]])]});}
            var Q13;
            {var subQ1=makeQuery(id+"F2.opExtrude","CAP_EDGE",EDGE,{"disambiguationData":[OSD([sQuery(id+"F1.wireOp",EDGE,"E5.6.0.1")])],"isStart":false});Q13=makeQuery(id+"F4.imprint","IMPRINT",FACE,{"disambiguationData":[TD([[makeQuery(id+"F4.imprint","IMPRINT",EDGE,{"derivedFrom":subQ1}),-1.0]])]});}
            var Q14;
            {var subQ1=makeQuery(id+"F2.opExtrude","CAP_EDGE",EDGE,{"disambiguationData":[OSD([sQuery(id+"F1.wireOp",EDGE,"E5.6.0.2")])],"isStart":false});Q14=makeQuery(id+"F4.imprint","IMPRINT",FACE,{"disambiguationData":[TD([[makeQuery(id+"F4.imprint","IMPRINT",EDGE,{"derivedFrom":subQ1}),-1.0]])]});}
            var Q15;
            {var subQ1=makeQuery(id+"F2.opExtrude","CAP_EDGE",EDGE,{"disambiguationData":[OSD([sQuery(id+"F1.wireOp",EDGE,"E5.7.0.1")])],"isStart":false});Q15=makeQuery(id+"F4.imprint","IMPRINT",FACE,{"disambiguationData":[TD([[makeQuery(id+"F4.imprint","IMPRINT",EDGE,{"derivedFrom":subQ1}),-1.0]])]});}
            var Q16;
            {var subQ1=makeQuery(id+"F2.opExtrude","CAP_EDGE",EDGE,{"disambiguationData":[OSD([sQuery(id+"F1.wireOp",EDGE,"E5.7.0.2")])],"isStart":false});Q16=makeQuery(id+"F4.imprint","IMPRINT",FACE,{"disambiguationData":[TD([[makeQuery(id+"F4.imprint","IMPRINT",EDGE,{"derivedFrom":subQ1}),-1.0]])]});}
            var Q17;
            {var subQ1=makeQuery(id+"F2.opExtrude","CAP_EDGE",EDGE,{"disambiguationData":[OSD([sQuery(id+"F1.wireOp",EDGE,"E5.8.0.1")])],"isStart":false});Q17=makeQuery(id+"F4.imprint","IMPRINT",FACE,{"disambiguationData":[TD([[makeQuery(id+"F4.imprint","IMPRINT",EDGE,{"derivedFrom":subQ1}),-1.0]])]});}
            var Q18;
            {var subQ2=sQuery(id+"F4.wireOp",EDGE,"E74.right");Q18=makeQuery(id+"F4.imprint","IMPRINT",FACE,{"disambiguationData":[TD([[makeQuery(id+"F4.imprint","IMPRINT",EDGE,{"derivedFrom":subQ2}),1.0]])]});}
            extrude(context, id + "F5", {"entities" : qUnion([Q0, Q1, Q2, Q3, Q4, Q5, Q6, Q7, Q8, Q9, Q10, Q11, Q12, Q13, Q14, Q15, Q16, Q17, Q18]), "depth" : (100 - getVariable(context, 'w')) * mm});
        }
        {
            var Q0;
            Q0=makeQuery(id+"F3.opExtrude","SWEPT_BODY",BODY,{"disambiguationData":[OSD([sQuery(id+"F1.wireOp",EDGE,"E4.bottom"),sQuery(id+"F1.wireOp",EDGE,"E4.top"),sQuery(id+"F1.wireOp",EDGE,"E4.left"),sQuery(id+"F1.wireOp",EDGE,"E4.right")])]});
            var Q1;
            Q1=makeQuery(id+"F3.opExtrude","SWEPT_BODY",BODY,{"disambiguationData":[OSD([sQuery(id+"F1.wireOp",EDGE,"E5.1.0.0"),sQuery(id+"F1.wireOp",EDGE,"E5.1.0.1"),sQuery(id+"F1.wireOp",EDGE,"E5.1.0.2"),sQuery(id+"F1.wireOp",EDGE,"E5.1.0.3")])]});
            var Q2;
            Q2=makeQuery(id+"F3.opExtrude","SWEPT_BODY",BODY,{"disambiguationData":[OSD([sQuery(id+"F1.wireOp",EDGE,"E5.2.0.0"),sQuery(id+"F1.wireOp",EDGE,"E5.2.0.1"),sQuery(id+"F1.wireOp",EDGE,"E5.2.0.2"),sQuery(id+"F1.wireOp",EDGE,"E5.2.0.3")])]});
            var Q3;
            Q3=makeQuery(id+"F3.opExtrude","SWEPT_BODY",BODY,{"disambiguationData":[OSD([sQuery(id+"F1.wireOp",EDGE,"E5.3.0.0"),sQuery(id+"F1.wireOp",EDGE,"E5.3.0.1"),sQuery(id+"F1.wireOp",EDGE,"E5.3.0.2"),sQuery(id+"F1.wireOp",EDGE,"E5.3.0.3")])]});
            var Q4;
            Q4=makeQuery(id+"F3.opExtrude","SWEPT_BODY",BODY,{"disambiguationData":[OSD([sQuery(id+"F1.wireOp",EDGE,"E5.4.0.0"),sQuery(id+"F1.wireOp",EDGE,"E5.4.0.1"),sQuery(id+"F1.wireOp",EDGE,"E5.4.0.2"),sQuery(id+"F1.wireOp",EDGE,"E5.4.0.3")])]});
            var Q5;
            Q5=makeQuery(id+"F3.opExtrude","SWEPT_BODY",BODY,{"disambiguationData":[OSD([sQuery(id+"F1.wireOp",EDGE,"E5.5.0.0"),sQuery(id+"F1.wireOp",EDGE,"E5.5.0.1"),sQuery(id+"F1.wireOp",EDGE,"E5.5.0.2"),sQuery(id+"F1.wireOp",EDGE,"E5.5.0.3")])]});
            var Q6;
            Q6=makeQuery(id+"F3.opExtrude","SWEPT_BODY",BODY,{"disambiguationData":[OSD([sQuery(id+"F1.wireOp",EDGE,"E5.6.0.0"),sQuery(id+"F1.wireOp",EDGE,"E5.6.0.1"),sQuery(id+"F1.wireOp",EDGE,"E5.6.0.2"),sQuery(id+"F1.wireOp",EDGE,"E5.6.0.3")])]});
            var Q7;
            Q7=makeQuery(id+"F3.opExtrude","SWEPT_BODY",BODY,{"disambiguationData":[OSD([sQuery(id+"F1.wireOp",EDGE,"E5.7.0.0"),sQuery(id+"F1.wireOp",EDGE,"E5.7.0.1"),sQuery(id+"F1.wireOp",EDGE,"E5.7.0.2"),sQuery(id+"F1.wireOp",EDGE,"E5.7.0.3")])]});
            var Q8;
            Q8=makeQuery(id+"F3.opExtrude","SWEPT_BODY",BODY,{"disambiguationData":[OSD([sQuery(id+"F1.wireOp",EDGE,"E5.8.0.0"),sQuery(id+"F1.wireOp",EDGE,"E5.8.0.1"),sQuery(id+"F1.wireOp",EDGE,"E5.8.0.2"),sQuery(id+"F1.wireOp",EDGE,"E45.MirrorCS")])]});
            var Q9;
            Q9=makeQuery(id+"F5.opExtrude","SWEPT_BODY",BODY,{"disambiguationData":[OSD([sQuery(id+"F4.wireOp",EDGE,"E74.bottom"),sQuery(id+"F4.wireOp",EDGE,"E74.top"),sQuery(id+"F4.wireOp",EDGE,"E74.left"),sQuery(id+"F4.wireOp",EDGE,"E74.right"),sQuery(id+"F4.wireOp",EDGE,"E75.bottom")])]});
            booleanBodies(context, id + "F6", {"operationType" : BooleanOperationType.UNION, "tools" : qUnion([Q0, Q1, Q2, Q3, Q4, Q5, Q6, Q7, Q8, Q9])});
        }
        {
            var Q0;
            Q0=makeQuery(id+"F6.opBoolean","MERGE",FACE,{"derivedFrom":[makeQuery(id+"F3.opExtrude","SWEPT_FACE",FACE,{"disambiguationData":[OSD([sQuery(id+"F1.wireOp",EDGE,"E4.bottom")])]}),makeQuery(id+"F3.opExtrude","SWEPT_FACE",FACE,{"disambiguationData":[OSD([sQuery(id+"F1.wireOp",EDGE,"E5.1.0.3")])]}),makeQuery(id+"F3.opExtrude","SWEPT_FACE",FACE,{"disambiguationData":[OSD([sQuery(id+"F1.wireOp",EDGE,"E5.2.0.3")])]}),makeQuery(id+"F3.opExtrude","SWEPT_FACE",FACE,{"disambiguationData":[OSD([sQuery(id+"F1.wireOp",EDGE,"E5.3.0.3")])]}),makeQuery(id+"F3.opExtrude","SWEPT_FACE",FACE,{"disambiguationData":[OSD([sQuery(id+"F1.wireOp",EDGE,"E5.4.0.3")])]}),makeQuery(id+"F3.opExtrude","SWEPT_FACE",FACE,{"disambiguationData":[OSD([sQuery(id+"F1.wireOp",EDGE,"E5.5.0.3")])]}),makeQuery(id+"F3.opExtrude","SWEPT_FACE",FACE,{"disambiguationData":[OSD([sQuery(id+"F1.wireOp",EDGE,"E5.6.0.3")])]}),makeQuery(id+"F3.opExtrude","SWEPT_FACE",FACE,{"disambiguationData":[OSD([sQuery(id+"F1.wireOp",EDGE,"E5.7.0.3")])]}),makeQuery(id+"F3.opExtrude","SWEPT_FACE",FACE,{"disambiguationData":[OSD([sQuery(id+"F1.wireOp",EDGE,"E45.MirrorCS")])]}),makeQuery(id+"F5.opExtrude","SWEPT_FACE",FACE,{"disambiguationData":[OSD([sQuery(id+"F4.wireOp",EDGE,"E74.top"),sQuery(id+"F4.wireOp",EDGE,"E75.bottom")])]})]});
            var sketch = newSketch(context, id + "F7", { "sketchPlane" : qUnion([Q0])});
            skLineSegment(sketch, "E76.bottom", {"start": v(-146, 8) * mm, "end": v(-142, 8) * mm});
            skLineSegment(sketch, "E76.top", {"start": v(-146, 18) * mm, "end": v(-142, 18) * mm});
            skLineSegment(sketch, "E76.left", {"start": v(-146, 8) * mm, "end": v(-146, 18) * mm});
            skLineSegment(sketch, "E76.right", {"start": v(-142, 8) * mm, "end": v(-142, 18) * mm});
            skLineSegment(sketch, "E77.1.0.0", {"start": v(-146, 23.6) * mm, "end": v(-146, 33.6) * mm});
            skLineSegment(sketch, "E77.1.0.1", {"start": v(-146, 33.6) * mm, "end": v(-142, 33.6) * mm});
            skLineSegment(sketch, "E77.1.0.2", {"start": v(-142, 23.6) * mm, "end": v(-142, 33.6) * mm});
            skLineSegment(sketch, "E77.1.0.3", {"start": v(-146, 23.6) * mm, "end": v(-142, 23.6) * mm});
            skLineSegment(sketch, "E77.2.0.0", {"start": v(-146, 39.2) * mm, "end": v(-146, 49.2) * mm});
            skLineSegment(sketch, "E77.2.0.1", {"start": v(-146, 49.2) * mm, "end": v(-142, 49.2) * mm});
            skLineSegment(sketch, "E77.2.0.2", {"start": v(-142, 39.2) * mm, "end": v(-142, 49.2) * mm});
            skLineSegment(sketch, "E77.2.0.3", {"start": v(-146, 39.2) * mm, "end": v(-142, 39.2) * mm});
            skLineSegment(sketch, "E77.3.0.0", {"start": v(-146, 54.8) * mm, "end": v(-146, 64.8) * mm});
            skLineSegment(sketch, "E77.3.0.1", {"start": v(-146, 64.8) * mm, "end": v(-142, 64.8) * mm});
            skLineSegment(sketch, "E77.3.0.2", {"start": v(-142, 54.8) * mm, "end": v(-142, 64.8) * mm});
            skLineSegment(sketch, "E77.3.0.3", {"start": v(-146, 54.8) * mm, "end": v(-142, 54.8) * mm});
            skLineSegment(sketch, "E77.4.0.0", {"start": v(-146, 70.4) * mm, "end": v(-146, 80.4) * mm});
            skLineSegment(sketch, "E77.4.0.1", {"start": v(-146, 80.4) * mm, "end": v(-142, 80.4) * mm});
            skLineSegment(sketch, "E77.4.0.2", {"start": v(-142, 70.4) * mm, "end": v(-142, 80.4) * mm});
            skLineSegment(sketch, "E77.4.0.3", {"start": v(-146, 70.4) * mm, "end": v(-142, 70.4) * mm});
            skLineSegment(sketch, "E77.5.0.0", {"start": v(-146, 86) * mm, "end": v(-146, 96) * mm});
            skLineSegment(sketch, "E77.5.0.1", {"start": v(-146, 96) * mm, "end": v(-142, 96) * mm});
            skLineSegment(sketch, "E77.5.0.2", {"start": v(-142, 86) * mm, "end": v(-142, 96) * mm});
            skLineSegment(sketch, "E77.5.0.3", {"start": v(-146, 86) * mm, "end": v(-142, 86) * mm});
            skLineSegment(sketch, "E77.direction1", {"start": v(-146, 8) * mm, "end": v(-146, 23.6) * mm, "construction": true});
            skLineSegment(sketch, "E78", {"start": v(-142, 4) * mm, "end": v(-142, 100) * mm, "construction": true});
            skLineSegment(sketch, "E79", {"start": v(0, 100) * mm, "end": v(0, 4) * mm, "construction": true});
            skPoint(sketch, "E79.endSnap0", {"position": v(0, 100) * mm});
            skLineSegment(sketch, "E80.MirrorCS", {"start": v(146, 70.4) * mm, "end": v(142, 70.4) * mm});
            skLineSegment(sketch, "E81.MirrorCS", {"start": v(146, 86) * mm, "end": v(142, 86) * mm});
            skLineSegment(sketch, "E82.MirrorCS", {"start": v(146, 96) * mm, "end": v(142, 96) * mm});
            skLineSegment(sketch, "E83.MirrorCS", {"start": v(146, 8) * mm, "end": v(142, 8) * mm});
            skLineSegment(sketch, "E84.MirrorCS", {"start": v(146, 64.8) * mm, "end": v(142, 64.8) * mm});
            skLineSegment(sketch, "E85.MirrorCS", {"start": v(146, 18) * mm, "end": v(142, 18) * mm});
            skLineSegment(sketch, "E86.MirrorCS", {"start": v(146, 49.2) * mm, "end": v(142, 49.2) * mm});
            skLineSegment(sketch, "E87.MirrorCS", {"start": v(146, 23.6) * mm, "end": v(142, 23.6) * mm});
            skLineSegment(sketch, "E88.MirrorCS", {"start": v(146, 80.4) * mm, "end": v(142, 80.4) * mm});
            skLineSegment(sketch, "E89.MirrorCS", {"start": v(146, 33.6) * mm, "end": v(142, 33.6) * mm});
            skLineSegment(sketch, "E90.MirrorCS", {"start": v(146, 54.8) * mm, "end": v(142, 54.8) * mm});
            skLineSegment(sketch, "E91.MirrorCS", {"start": v(146, 39.2) * mm, "end": v(142, 39.2) * mm});
            skLineSegment(sketch, "E92.MirrorCS", {"start": v(146, 23.6) * mm, "end": v(146, 33.6) * mm});
            skLineSegment(sketch, "E93.MirrorCS", {"start": v(146, 8) * mm, "end": v(146, 18) * mm});
            skLineSegment(sketch, "E94.MirrorCS", {"start": v(142, 39.2) * mm, "end": v(142, 49.2) * mm});
            skLineSegment(sketch, "E95.MirrorCS", {"start": v(146, 86) * mm, "end": v(146, 96) * mm});
            skLineSegment(sketch, "E96.MirrorCS", {"start": v(142, 23.6) * mm, "end": v(142, 33.6) * mm});
            skLineSegment(sketch, "E97.MirrorCS", {"start": v(142, 86) * mm, "end": v(142, 96) * mm});
            skLineSegment(sketch, "E98.MirrorCS", {"start": v(142, 8) * mm, "end": v(142, 18) * mm});
            skLineSegment(sketch, "E99.MirrorCS", {"start": v(146, 8) * mm, "end": v(146, 23.6) * mm, "construction": true});
            skLineSegment(sketch, "E100.MirrorCS", {"start": v(146, 70.4) * mm, "end": v(146, 80.4) * mm});
            skLineSegment(sketch, "E101.MirrorCS", {"start": v(142, 54.8) * mm, "end": v(142, 64.8) * mm});
            skLineSegment(sketch, "E102.MirrorCS", {"start": v(146, 39.2) * mm, "end": v(146, 49.2) * mm});
            skLineSegment(sketch, "E103.MirrorCS", {"start": v(142, 70.4) * mm, "end": v(142, 80.4) * mm});
            skLineSegment(sketch, "E104.MirrorCS", {"start": v(146, 54.8) * mm, "end": v(146, 64.8) * mm});
            skLineSegment(sketch, "E105.MirrorCS", {"start": v(142, 4) * mm, "end": v(142, 100) * mm, "construction": true});
            skSolve(sketch);
        }
        {
            var Q0;
            Q0=makeQuery(id+"F7.imprint","IMPRINT",FACE,{"disambiguationData":[TD([[makeQuery(id+"F7.imprint","IMPRINT",EDGE,{"derivedFrom":sQuery(id+"F7.wireOp",EDGE,"E77.5.0.0")}),-1.0]])]});
            var Q1;
            Q1=makeQuery(id+"F7.imprint","IMPRINT",FACE,{"disambiguationData":[TD([[makeQuery(id+"F7.imprint","IMPRINT",EDGE,{"derivedFrom":sQuery(id+"F7.wireOp",EDGE,"E77.4.0.0")}),-1.0]])]});
            var Q2;
            Q2=makeQuery(id+"F7.imprint","IMPRINT",FACE,{"disambiguationData":[TD([[makeQuery(id+"F7.imprint","IMPRINT",EDGE,{"derivedFrom":sQuery(id+"F7.wireOp",EDGE,"E77.3.0.0")}),-1.0]])]});
            var Q3;
            Q3=makeQuery(id+"F7.imprint","IMPRINT",FACE,{"disambiguationData":[TD([[makeQuery(id+"F7.imprint","IMPRINT",EDGE,{"derivedFrom":sQuery(id+"F7.wireOp",EDGE,"E77.2.0.0")}),-1.0]])]});
            var Q4;
            Q4=makeQuery(id+"F7.imprint","IMPRINT",FACE,{"disambiguationData":[TD([[makeQuery(id+"F7.imprint","IMPRINT",EDGE,{"derivedFrom":sQuery(id+"F7.wireOp",EDGE,"E77.1.0.0")}),-1.0]])]});
            var Q5;
            Q5=makeQuery(id+"F7.imprint","IMPRINT",FACE,{"disambiguationData":[TD([[makeQuery(id+"F7.imprint","IMPRINT",EDGE,{"derivedFrom":sQuery(id+"F7.wireOp",EDGE,"E76.bottom")}),1.0]])]});
            var Q6;
            Q6=makeQuery(id+"F7.imprint","IMPRINT",FACE,{"disambiguationData":[TD([[makeQuery(id+"F7.imprint","IMPRINT",EDGE,{"derivedFrom":sQuery(id+"F7.wireOp",EDGE,"E81.MirrorCS")}),-1.0]])]});
            var Q7;
            Q7=makeQuery(id+"F7.imprint","IMPRINT",FACE,{"disambiguationData":[TD([[makeQuery(id+"F7.imprint","IMPRINT",EDGE,{"derivedFrom":sQuery(id+"F7.wireOp",EDGE,"E80.MirrorCS")}),-1.0]])]});
            var Q8;
            Q8=makeQuery(id+"F7.imprint","IMPRINT",FACE,{"disambiguationData":[TD([[makeQuery(id+"F7.imprint","IMPRINT",EDGE,{"derivedFrom":sQuery(id+"F7.wireOp",EDGE,"E84.MirrorCS")}),1.0]])]});
            var Q9;
            Q9=makeQuery(id+"F7.imprint","IMPRINT",FACE,{"disambiguationData":[TD([[makeQuery(id+"F7.imprint","IMPRINT",EDGE,{"derivedFrom":sQuery(id+"F7.wireOp",EDGE,"E86.MirrorCS")}),1.0]])]});
            var Q10;
            Q10=makeQuery(id+"F7.imprint","IMPRINT",FACE,{"disambiguationData":[TD([[makeQuery(id+"F7.imprint","IMPRINT",EDGE,{"derivedFrom":sQuery(id+"F7.wireOp",EDGE,"E87.MirrorCS")}),-1.0]])]});
            var Q11;
            Q11=makeQuery(id+"F7.imprint","IMPRINT",FACE,{"disambiguationData":[TD([[makeQuery(id+"F7.imprint","IMPRINT",EDGE,{"derivedFrom":sQuery(id+"F7.wireOp",EDGE,"E83.MirrorCS")}),-1.0]])]});
            extrude(context, id + "F8", {"entities" : qUnion([Q0, Q1, Q2, Q3, Q4, Q5, Q6, Q7, Q8, Q9, Q10, Q11]), "operationType" : NewBodyOperationType.REMOVE, "endBound" : BoundingType.THROUGH_ALL, "oppositeDirection" : true, "depth" : 25 * mm});
        }
        {
            var Q0;
            Q0=makeQuery(id+"F7.imprint","IMPRINT",FACE,{"disambiguationData":[TD([[makeQuery(id+"F7.imprint","IMPRINT",EDGE,{"derivedFrom":sQuery(id+"F7.wireOp",EDGE,"E77.3.0.0")}),-1.0]])]});
            var Q1;
            Q1=makeQuery(id+"F7.imprint","IMPRINT",FACE,{"disambiguationData":[TD([[makeQuery(id+"F7.imprint","IMPRINT",EDGE,{"derivedFrom":sQuery(id+"F7.wireOp",EDGE,"E77.4.0.0")}),-1.0]])]});
            var Q2;
            Q2=makeQuery(id+"F7.imprint","IMPRINT",FACE,{"disambiguationData":[TD([[makeQuery(id+"F7.imprint","IMPRINT",EDGE,{"derivedFrom":sQuery(id+"F7.wireOp",EDGE,"E77.5.0.0")}),-1.0]])]});
            var Q3;
            Q3=makeQuery(id+"F7.imprint","IMPRINT",FACE,{"disambiguationData":[TD([[makeQuery(id+"F7.imprint","IMPRINT",EDGE,{"derivedFrom":sQuery(id+"F7.wireOp",EDGE,"E77.2.0.0")}),-1.0]])]});
            var Q4;
            Q4=makeQuery(id+"F7.imprint","IMPRINT",FACE,{"disambiguationData":[TD([[makeQuery(id+"F7.imprint","IMPRINT",EDGE,{"derivedFrom":sQuery(id+"F7.wireOp",EDGE,"E77.1.0.0")}),-1.0]])]});
            var Q5;
            Q5=makeQuery(id+"F7.imprint","IMPRINT",FACE,{"disambiguationData":[TD([[makeQuery(id+"F7.imprint","IMPRINT",EDGE,{"derivedFrom":sQuery(id+"F7.wireOp",EDGE,"E76.bottom")}),1.0]])]});
            extrude(context, id + "F9", {"entities" : qUnion([Q0, Q1, Q2, Q3, Q4, Q5]), "oppositeDirection" : true, "depth" : (getVariable(context, 'w')) * mm});
        }
        {
            var Q0;
            Q0=makeQuery(id+"F1.imprint","IMPRINT",FACE,{"disambiguationData":[TD([[makeQuery(id+"F1.imprint","IMPRINT",EDGE,{"derivedFrom":sQuery(id+"F1.wireOp",EDGE,"E43.bottom")}),-1.0]])]});
            var Q1;
            Q1=makeQuery(id+"F1.imprint","IMPRINT",FACE,{"disambiguationData":[TD([[makeQuery(id+"F1.imprint","IMPRINT",EDGE,{"derivedFrom":sQuery(id+"F1.wireOp",EDGE,"E44.1.0.0")}),1.0]])]});
            var Q2;
            Q2=makeQuery(id+"F1.imprint","IMPRINT",FACE,{"disambiguationData":[TD([[makeQuery(id+"F1.imprint","IMPRINT",EDGE,{"derivedFrom":sQuery(id+"F1.wireOp",EDGE,"E44.2.0.0")}),1.0]])]});
            var Q3;
            Q3=makeQuery(id+"F1.imprint","IMPRINT",FACE,{"disambiguationData":[TD([[makeQuery(id+"F1.imprint","IMPRINT",EDGE,{"derivedFrom":sQuery(id+"F1.wireOp",EDGE,"E44.0.1.0")}),1.0]])]});
            var Q4;
            Q4=makeQuery(id+"F1.imprint","IMPRINT",FACE,{"disambiguationData":[TD([[makeQuery(id+"F1.imprint","IMPRINT",EDGE,{"derivedFrom":sQuery(id+"F1.wireOp",EDGE,"E44.1.1.0")}),1.0]])]});
            var Q5;
            Q5=makeQuery(id+"F1.imprint","IMPRINT",FACE,{"disambiguationData":[TD([[makeQuery(id+"F1.imprint","IMPRINT",EDGE,{"derivedFrom":sQuery(id+"F1.wireOp",EDGE,"E44.2.1.0")}),1.0]])]});
            extrude(context, id + "F10", {"entities" : qUnion([Q0, Q1, Q2, Q3, Q4, Q5]), "depth" : (getVariable(context, 'w')) * mm});
        }
        {
            var Q0;
            {var subQ0=sQuery(id+"F4.wireOp",EDGE,"E75.bottom");Q0=makeQuery(id+"F4.imprint","IMPRINT",FACE,{"disambiguationData":[TD([[makeQuery(id+"F4.imprint","IMPRINT",EDGE,{"derivedFrom":subQ0}),1.0]])]});}
            var Q1;
            {var subQ1=makeQuery(id+"F2.opExtrude","CAP_EDGE",EDGE,{"disambiguationData":[OSD([sQuery(id+"F1.wireOp",EDGE,"E43.bottom")])],"isStart":false});Q1=makeQuery(id+"F4.imprint","IMPRINT",FACE,{"disambiguationData":[TD([[makeQuery(id+"F4.imprint","IMPRINT",EDGE,{"derivedFrom":subQ1}),-1.0]])]});}
            var Q2;
            {var subQ1=makeQuery(id+"F2.opExtrude","CAP_EDGE",EDGE,{"disambiguationData":[OSD([sQuery(id+"F1.wireOp",EDGE,"E43.top")])],"isStart":false});Q2=makeQuery(id+"F4.imprint","IMPRINT",FACE,{"disambiguationData":[TD([[makeQuery(id+"F4.imprint","IMPRINT",EDGE,{"derivedFrom":subQ1}),-1.0]])]});}
            var Q3;
            {var subQ1=makeQuery(id+"F2.opExtrude","CAP_EDGE",EDGE,{"disambiguationData":[OSD([sQuery(id+"F1.wireOp",EDGE,"E44.1.0.1")])],"isStart":false});Q3=makeQuery(id+"F4.imprint","IMPRINT",FACE,{"disambiguationData":[TD([[makeQuery(id+"F4.imprint","IMPRINT",EDGE,{"derivedFrom":subQ1}),-1.0]])]});}
            var Q4;
            {var subQ1=makeQuery(id+"F2.opExtrude","CAP_EDGE",EDGE,{"disambiguationData":[OSD([sQuery(id+"F1.wireOp",EDGE,"E44.1.0.2")])],"isStart":false});Q4=makeQuery(id+"F4.imprint","IMPRINT",FACE,{"disambiguationData":[TD([[makeQuery(id+"F4.imprint","IMPRINT",EDGE,{"derivedFrom":subQ1}),-1.0]])]});}
            var Q5;
            {var subQ1=makeQuery(id+"F2.opExtrude","CAP_EDGE",EDGE,{"disambiguationData":[OSD([sQuery(id+"F1.wireOp",EDGE,"E44.2.0.1")])],"isStart":false});Q5=makeQuery(id+"F4.imprint","IMPRINT",FACE,{"disambiguationData":[TD([[makeQuery(id+"F4.imprint","IMPRINT",EDGE,{"derivedFrom":subQ1}),-1.0]])]});}
            var Q6;
            {var subQ0=makeQuery(id+"F2.opExtrude","CAP_EDGE",EDGE,{"disambiguationData":[OSD([sQuery(id+"F1.wireOp",EDGE,"E44.0.1.1")])],"isStart":false});Q6=makeQuery(id+"F4.imprint","IMPRINT",FACE,{"disambiguationData":[TD([[makeQuery(id+"F4.imprint","IMPRINT",EDGE,{"derivedFrom":subQ0}),1.0]])]});}
            var Q7;
            {var subQ0=sQuery(id+"F4.wireOp",EDGE,"E75.top");Q7=makeQuery(id+"F4.imprint","IMPRINT",FACE,{"disambiguationData":[TD([[makeQuery(id+"F4.imprint","IMPRINT",EDGE,{"derivedFrom":subQ0}),-1.0]])]});}
            var Q8;
            {var subQ1=makeQuery(id+"F2.opExtrude","CAP_EDGE",EDGE,{"disambiguationData":[OSD([sQuery(id+"F1.wireOp",EDGE,"E44.2.1.1")])],"isStart":false});Q8=makeQuery(id+"F4.imprint","IMPRINT",FACE,{"disambiguationData":[TD([[makeQuery(id+"F4.imprint","IMPRINT",EDGE,{"derivedFrom":subQ1}),-1.0]])]});}
            var Q9;
            {var subQ1=makeQuery(id+"F2.opExtrude","CAP_EDGE",EDGE,{"disambiguationData":[OSD([sQuery(id+"F1.wireOp",EDGE,"E44.0.1.1")])],"isStart":false});Q9=makeQuery(id+"F4.imprint","IMPRINT",FACE,{"disambiguationData":[TD([[makeQuery(id+"F4.imprint","IMPRINT",EDGE,{"derivedFrom":subQ1}),-1.0]])]});}
            var Q10;
            {var subQ1=makeQuery(id+"F2.opExtrude","CAP_EDGE",EDGE,{"disambiguationData":[OSD([sQuery(id+"F1.wireOp",EDGE,"E44.0.1.2")])],"isStart":false});Q10=makeQuery(id+"F4.imprint","IMPRINT",FACE,{"disambiguationData":[TD([[makeQuery(id+"F4.imprint","IMPRINT",EDGE,{"derivedFrom":subQ1}),-1.0]])]});}
            var Q11;
            {var subQ1=makeQuery(id+"F2.opExtrude","CAP_EDGE",EDGE,{"disambiguationData":[OSD([sQuery(id+"F1.wireOp",EDGE,"E44.1.1.1")])],"isStart":false});Q11=makeQuery(id+"F4.imprint","IMPRINT",FACE,{"disambiguationData":[TD([[makeQuery(id+"F4.imprint","IMPRINT",EDGE,{"derivedFrom":subQ1}),-1.0]])]});}
            var Q12;
            {var subQ1=makeQuery(id+"F2.opExtrude","CAP_EDGE",EDGE,{"disambiguationData":[OSD([sQuery(id+"F1.wireOp",EDGE,"E44.1.1.2")])],"isStart":false});Q12=makeQuery(id+"F4.imprint","IMPRINT",FACE,{"disambiguationData":[TD([[makeQuery(id+"F4.imprint","IMPRINT",EDGE,{"derivedFrom":subQ1}),-1.0]])]});}
            extrude(context, id + "F11", {"entities" : qUnion([Q0, Q1, Q2, Q3, Q4, Q5, Q6, Q7, Q8, Q9, Q10, Q11, Q12]), "depth" : (100 - getVariable(context, 'w')) * mm});
        }
        {
            var Q0;
            Q0=makeQuery(id+"F9.opExtrude","SWEPT_BODY",BODY,{"disambiguationData":[OSD([sQuery(id+"F7.wireOp",EDGE,"E76.bottom"),sQuery(id+"F7.wireOp",EDGE,"E76.top"),sQuery(id+"F7.wireOp",EDGE,"E76.left"),sQuery(id+"F7.wireOp",EDGE,"E76.right")])]});
            var Q1;
            Q1=makeQuery(id+"F9.opExtrude","SWEPT_BODY",BODY,{"disambiguationData":[OSD([sQuery(id+"F7.wireOp",EDGE,"E77.1.0.0"),sQuery(id+"F7.wireOp",EDGE,"E77.1.0.1"),sQuery(id+"F7.wireOp",EDGE,"E77.1.0.2"),sQuery(id+"F7.wireOp",EDGE,"E77.1.0.3")])]});
            var Q2;
            Q2=makeQuery(id+"F9.opExtrude","SWEPT_BODY",BODY,{"disambiguationData":[OSD([sQuery(id+"F7.wireOp",EDGE,"E77.2.0.0"),sQuery(id+"F7.wireOp",EDGE,"E77.2.0.1"),sQuery(id+"F7.wireOp",EDGE,"E77.2.0.2"),sQuery(id+"F7.wireOp",EDGE,"E77.2.0.3")])]});
            var Q3;
            Q3=makeQuery(id+"F9.opExtrude","SWEPT_BODY",BODY,{"disambiguationData":[OSD([sQuery(id+"F7.wireOp",EDGE,"E77.3.0.0"),sQuery(id+"F7.wireOp",EDGE,"E77.3.0.1"),sQuery(id+"F7.wireOp",EDGE,"E77.3.0.2"),sQuery(id+"F7.wireOp",EDGE,"E77.3.0.3")])]});
            var Q4;
            Q4=makeQuery(id+"F9.opExtrude","SWEPT_BODY",BODY,{"disambiguationData":[OSD([sQuery(id+"F7.wireOp",EDGE,"E77.4.0.0"),sQuery(id+"F7.wireOp",EDGE,"E77.4.0.1"),sQuery(id+"F7.wireOp",EDGE,"E77.4.0.2"),sQuery(id+"F7.wireOp",EDGE,"E77.4.0.3")])]});
            var Q5;
            Q5=makeQuery(id+"F9.opExtrude","SWEPT_BODY",BODY,{"disambiguationData":[OSD([sQuery(id+"F7.wireOp",EDGE,"E77.5.0.0"),sQuery(id+"F7.wireOp",EDGE,"E77.5.0.1"),sQuery(id+"F7.wireOp",EDGE,"E77.5.0.2"),sQuery(id+"F7.wireOp",EDGE,"E77.5.0.3")])]});
            var Q6;
            Q6=qCreatedBy(makeId("Front.planeOp"),FACE);
            mirror(context, id + "F12", {"operationType" : NewBodyOperationType.ADD, "entities" : qUnion([Q0, Q1, Q2, Q3, Q4, Q5]), "mirrorPlane" : qUnion([Q6])});
        }
    });
